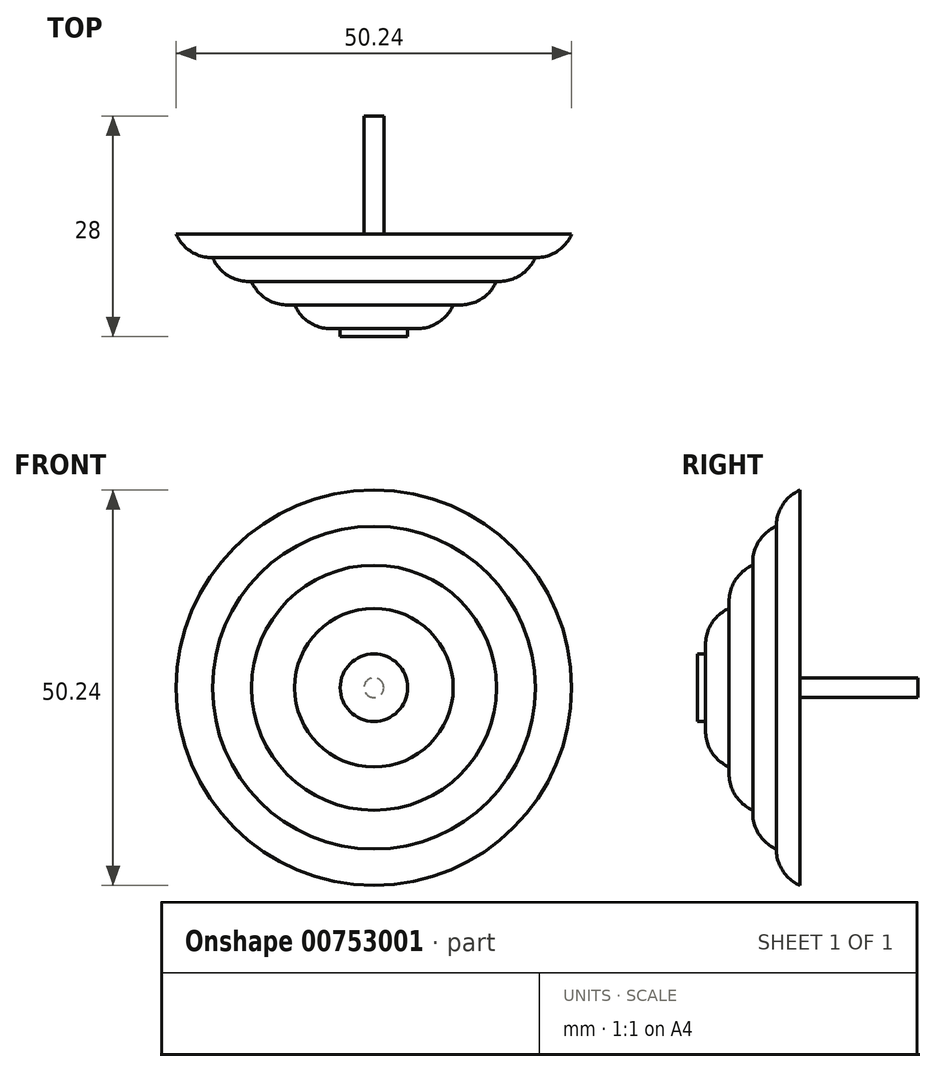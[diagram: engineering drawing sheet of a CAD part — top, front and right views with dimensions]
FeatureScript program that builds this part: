
annotation { "Feature Type Name" : "Feature", "Feature Type Description" : "" }
export const myFeature = defineFeature(function(context is Context, id is Id, definition is map)
    precondition{}
    {
        {
            var Q0;
            Q0=qCreatedBy(makeId("Front.planeOp"),FACE);
            var sketch = newSketch(context, id + "F0", { "sketchPlane" : qUnion([Q0])});
            skCircle(sketch, "E0", {"center": v(0, 0) * mm, "radius": 25.12 * mm});
            skCircle(sketch, "E1", {"center": v(0, 0) * mm, "radius": 20.5 * mm});
            skCircle(sketch, "E2", {"center": v(0, 0) * mm, "radius": 15.56 * mm});
            skCircle(sketch, "E3", {"center": v(0, 0) * mm, "radius": 10.08 * mm});
            skCircle(sketch, "E4", {"center": v(0, 0) * mm, "radius": 4.28 * mm});
            skCircle(sketch, "E5", {"center": v(0, 0) * mm, "radius": 1.25 * mm});
            skSolve(sketch);
        }
        {
            var Q0;
            Q0=makeQuery(id+"F0.imprint","IMPRINT",FACE,{"disambiguationData":[TD([[makeQuery(id+"F0.imprint","IMPRINT",EDGE,{"derivedFrom":sQuery(id+"F0.wireOp",EDGE,"E0")}),1.0]])]});
            extrude(context, id + "F1", {"entities" : qUnion([Q0]), "depth" : 3 * mm, "offsetDistance" : 25 * mm});
        }
        {
            var Q0;
            Q0=makeQuery(id+"F0.imprint","IMPRINT",FACE,{"disambiguationData":[TD([[makeQuery(id+"F0.imprint","IMPRINT",EDGE,{"derivedFrom":sQuery(id+"F0.wireOp",EDGE,"E1")}),1.0]])]});
            extrude(context, id + "F2", {"entities" : qUnion([Q0]), "operationType" : NewBodyOperationType.ADD, "depth" : 6 * mm, "offsetDistance" : 25 * mm});
        }
        {
            var Q0;
            Q0=makeQuery(id+"F0.imprint","IMPRINT",FACE,{"disambiguationData":[TD([[makeQuery(id+"F0.imprint","IMPRINT",EDGE,{"derivedFrom":sQuery(id+"F0.wireOp",EDGE,"E2")}),1.0]])]});
            extrude(context, id + "F3", {"entities" : qUnion([Q0]), "operationType" : NewBodyOperationType.ADD, "depth" : 9 * mm, "offsetDistance" : 25 * mm});
        }
        {
            var Q0;
            Q0=makeQuery(id+"F0.imprint","IMPRINT",FACE,{"disambiguationData":[TD([[makeQuery(id+"F0.imprint","IMPRINT",EDGE,{"derivedFrom":sQuery(id+"F0.wireOp",EDGE,"E3")}),1.0]])]});
            extrude(context, id + "F4", {"entities" : qUnion([Q0]), "operationType" : NewBodyOperationType.ADD, "depth" : 12 * mm, "offsetDistance" : 25 * mm});
        }
        {
            var Q0;
            Q0=makeQuery(id+"F0.imprint","IMPRINT",FACE,{"disambiguationData":[TD([[makeQuery(id+"F0.imprint","IMPRINT",EDGE,{"derivedFrom":sQuery(id+"F0.wireOp",EDGE,"E4")}),1.0]])]});
            extrude(context, id + "F5", {"entities" : qUnion([Q0]), "operationType" : NewBodyOperationType.ADD, "depth" : 13 * mm, "offsetDistance" : 25 * mm});
        }
        {
            var Q0;
            Q0=makeQuery(id+"F0.imprint","IMPRINT",FACE,{"disambiguationData":[TD([[makeQuery(id+"F0.imprint","IMPRINT",EDGE,{"derivedFrom":sQuery(id+"F0.wireOp",EDGE,"E5")}),1.0]])]});
            extrude(context, id + "F6", {"entities" : qUnion([Q0]), "operationType" : NewBodyOperationType.ADD, "depth" : 13 * mm, "offsetDistance" : 25 * mm});
        }
        {
            var Q0;
            Q0=makeQuery(id+"F0.imprint","IMPRINT",FACE,{"disambiguationData":[TD([[makeQuery(id+"F0.imprint","IMPRINT",EDGE,{"derivedFrom":sQuery(id+"F0.wireOp",EDGE,"E5")}),1.0]])]});
            extrude(context, id + "F7", {"entities" : qUnion([Q0]), "operationType" : NewBodyOperationType.ADD, "oppositeDirection" : true, "depth" : 15 * mm, "offsetDistance" : 25 * mm});
        }
        {
            var Q0;
            Q0=makeQuery(id+"F1.opExtrude","CAP_EDGE",EDGE,{"disambiguationData":[OSD([sQuery(id+"F0.wireOp",EDGE,"E0")])],"isStart":false});
            var Q1;
            Q1=makeQuery(id+"F2.opExtrude","CAP_EDGE",EDGE,{"disambiguationData":[OSD([sQuery(id+"F0.wireOp",EDGE,"E1")])],"isStart":false});
            var Q2;
            Q2=makeQuery(id+"F3.opExtrude","CAP_EDGE",EDGE,{"disambiguationData":[OSD([sQuery(id+"F0.wireOp",EDGE,"E2")])],"isStart":false});
            var Q3;
            Q3=makeQuery(id+"F4.opExtrude","CAP_EDGE",EDGE,{"disambiguationData":[OSD([sQuery(id+"F0.wireOp",EDGE,"E3")])],"isStart":false});
            fillet(context, id + "F8", {"entities" : qUnion([Q0, Q1, Q2, Q3]), "radius" : 5 * mm, "tangentPropagation" : true, "allowEdgeOverflow" : false});
        }
    });
